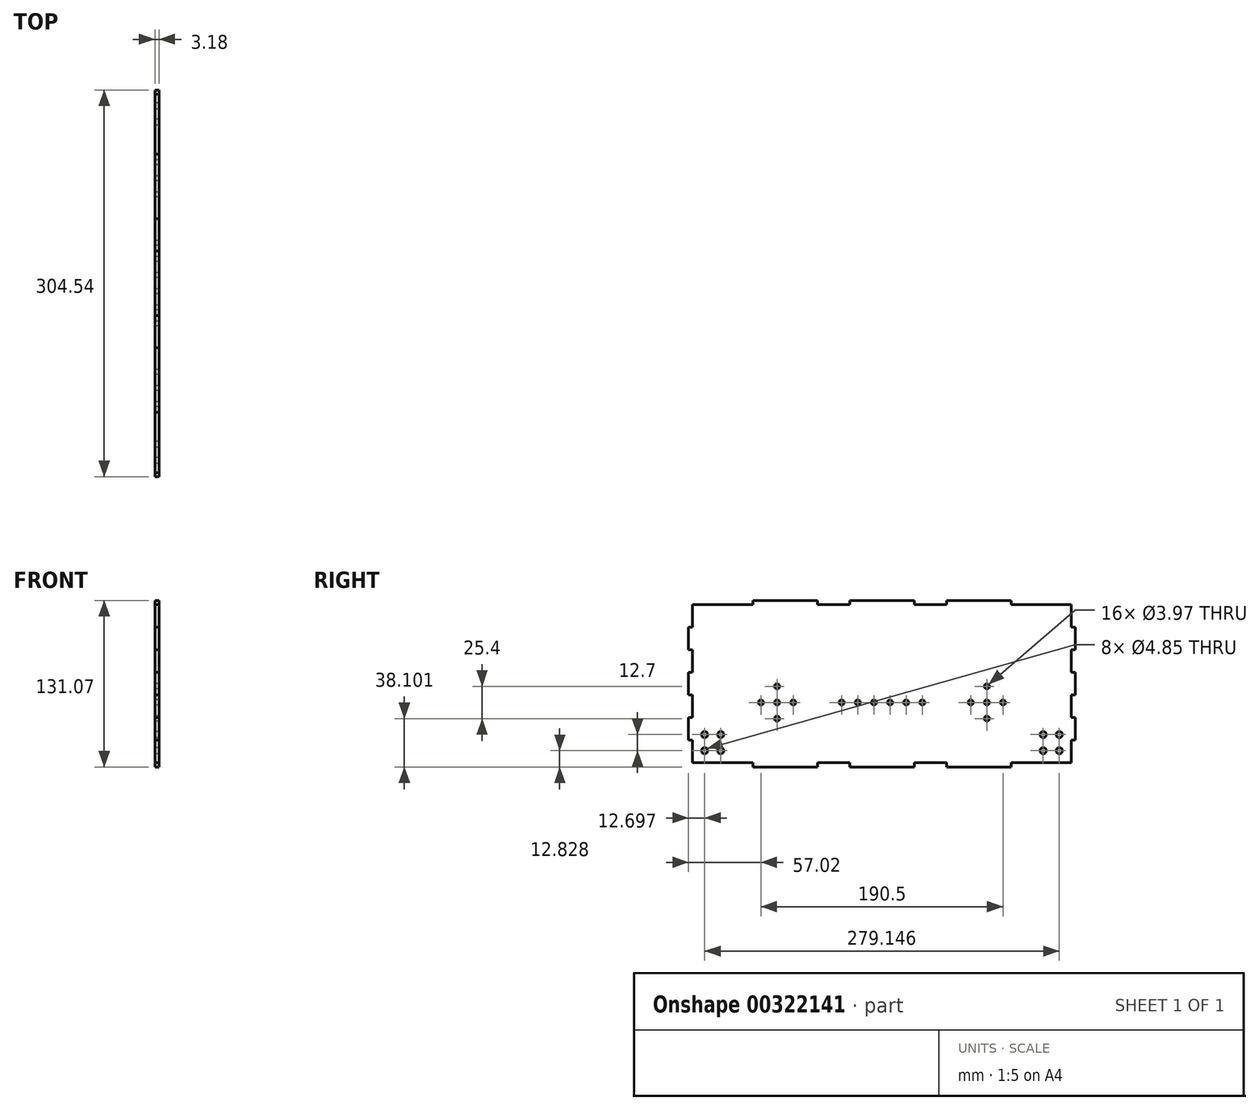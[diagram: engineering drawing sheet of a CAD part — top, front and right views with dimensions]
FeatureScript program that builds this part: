
annotation { "Feature Type Name" : "Feature", "Feature Type Description" : "" }
export const myFeature = defineFeature(function(context is Context, id is Id, definition is map)
    precondition{}
    {
        {
            var Q0;
            Q0=qCreatedBy(makeId("Right.planeOp"),FACE);
            var sketch = newSketch(context, id + "F0", { "sketchPlane" : qUnion([Q0])});
            skLineSegment(sketch, "E0.MirrorCS", {"start": v(-50.8, -81.48) * mm, "end": v(-50.8, -78.18) * mm});
            skLineSegment(sketch, "E1.MirrorCS", {"start": v(25.4, -81.48) * mm, "end": v(25.4, -78.18) * mm});
            skLineSegment(sketch, "E2.MirrorCS", {"start": v(50.8, -81.48) * mm, "end": v(50.8, -78.18) * mm});
            skLineSegment(sketch, "E3.MirrorCS", {"start": v(101.6, -81.48) * mm, "end": v(101.6, -78.18) * mm});
            skLineSegment(sketch, "E4.MirrorCS", {"start": v(-25.4, -81.48) * mm, "end": v(-25.4, -78.18) * mm});
            skLineSegment(sketch, "E5.MirrorCS", {"start": v(101.6, -81.48) * mm, "end": v(50.8, -81.48) * mm});
            skLineSegment(sketch, "E6.MirrorCS", {"start": v(-25.4, -81.48) * mm, "end": v(25.4, -81.48) * mm});
            skLineSegment(sketch, "E7.MirrorCS", {"start": v(-50.8, -81.48) * mm, "end": v(-25.4, -81.48) * mm, "construction": true});
            skLineSegment(sketch, "E8.MirrorCS", {"start": v(-101.6, -81.48) * mm, "end": v(-50.8, -81.48) * mm});
            skLineSegment(sketch, "E9.MirrorCS", {"start": v(-101.6, -81.48) * mm, "end": v(-101.6, -78.18) * mm});
            skLineSegment(sketch, "E10", {"start": v(101.6, -78.18) * mm, "end": v(149.1, -78.18) * mm});
            skLineSegment(sketch, "E11", {"start": v(50.8, -78.18) * mm, "end": v(25.4, -78.18) * mm});
            skLineSegment(sketch, "E12", {"start": v(-25.4, -78.18) * mm, "end": v(-50.8, -78.18) * mm});
            skLineSegment(sketch, "E13.MirrorCS", {"start": v(-101.6, -78.18) * mm, "end": v(-149.1, -78.18) * mm});
            skLineSegment(sketch, "E14", {"start": v(-149.1, -78.18) * mm, "end": v(-149.1, -60.4) * mm});
            skLineSegment(sketch, "E15", {"start": v(149.1, 46.28) * mm, "end": v(149.1, 28.5) * mm});
            skLineSegment(sketch, "E16", {"start": v(149.1, -15.95) * mm, "end": v(-149.1, -15.95) * mm, "construction": true});
            skLineSegment(sketch, "E17.MirrorCS", {"start": v(-50.8, 49.59) * mm, "end": v(-25.4, 49.59) * mm, "construction": true});
            skLineSegment(sketch, "E18.MirrorCS", {"start": v(-101.6, 49.59) * mm, "end": v(-101.6, 46.28) * mm});
            skLineSegment(sketch, "E19.MirrorCS", {"start": v(50.8, 46.28) * mm, "end": v(25.4, 46.28) * mm});
            skLineSegment(sketch, "E20.MirrorCS", {"start": v(25.4, 49.59) * mm, "end": v(25.4, 46.28) * mm});
            skLineSegment(sketch, "E21.MirrorCS", {"start": v(101.6, 49.59) * mm, "end": v(101.6, 46.28) * mm});
            skLineSegment(sketch, "E22.MirrorCS", {"start": v(101.6, 49.59) * mm, "end": v(50.8, 49.59) * mm});
            skLineSegment(sketch, "E23.MirrorCS", {"start": v(-101.6, 49.59) * mm, "end": v(-50.8, 49.59) * mm});
            skLineSegment(sketch, "E24.MirrorCS", {"start": v(-25.4, 46.28) * mm, "end": v(-50.8, 46.28) * mm});
            skLineSegment(sketch, "E25.MirrorCS", {"start": v(-101.6, 46.28) * mm, "end": v(-149.1, 46.28) * mm});
            skLineSegment(sketch, "E26.MirrorCS", {"start": v(101.6, 46.28) * mm, "end": v(149.1, 46.28) * mm});
            skLineSegment(sketch, "E27.MirrorCS", {"start": v(-50.8, 49.59) * mm, "end": v(-50.8, 46.28) * mm});
            skLineSegment(sketch, "E28.MirrorCS", {"start": v(50.8, 49.59) * mm, "end": v(50.8, 46.28) * mm});
            skLineSegment(sketch, "E29.MirrorCS", {"start": v(-25.4, 49.59) * mm, "end": v(-25.4, 46.28) * mm});
            skLineSegment(sketch, "E30.MirrorCS", {"start": v(-25.4, 49.59) * mm, "end": v(25.4, 49.59) * mm});
            skPoint(sketch, "E31", {"position": v(0, -30.68) * mm});
            skPoint(sketch, "E32", {"position": v(0, -15.95) * mm});
            skCircle(sketch, "E33", {"center": v(31.75, -30.68) * mm, "radius": 1.98 * mm});
            skCircle(sketch, "E34.MirrorC", {"center": v(-31.75, -30.68) * mm, "radius": 1.98 * mm});
            skCircle(sketch, "E35", {"center": v(82.55, -30.68) * mm, "radius": 1.98 * mm});
            skCircle(sketch, "E36.MirrorC", {"center": v(-82.55, -30.68) * mm, "radius": 1.98 * mm});
            skLineSegment(sketch, "E37", {"start": v(-149.1, 28.5) * mm, "end": v(-152.27, 28.5) * mm});
            skLineSegment(sketch, "E38", {"start": v(-152.27, 28.5) * mm, "end": v(-152.27, 10.72) * mm});
            skLineSegment(sketch, "E39", {"start": v(-152.27, 10.72) * mm, "end": v(-149.1, 10.72) * mm});
            skLineSegment(sketch, "E40", {"start": v(-149.1, -7.06) * mm, "end": v(-152.27, -7.06) * mm});
            skLineSegment(sketch, "E41", {"start": v(-152.27, -7.06) * mm, "end": v(-152.27, -24.84) * mm});
            skLineSegment(sketch, "E42", {"start": v(-152.27, -24.84) * mm, "end": v(-149.1, -24.84) * mm});
            skLineSegment(sketch, "E43", {"start": v(-149.1, -42.62) * mm, "end": v(-152.27, -42.62) * mm});
            skLineSegment(sketch, "E44", {"start": v(-152.27, -42.62) * mm, "end": v(-152.27, -60.4) * mm});
            skLineSegment(sketch, "E45", {"start": v(-152.27, -60.4) * mm, "end": v(-149.1, -60.4) * mm});
            skLineSegment(sketch, "E46", {"start": v(-152.27, 10.72) * mm, "end": v(-152.27, -7.06) * mm, "construction": true});
            skLineSegment(sketch, "E47", {"start": v(-152.27, -24.84) * mm, "end": v(-152.27, -42.62) * mm, "construction": true});
            skLineSegment(sketch, "E48", {"start": v(-152.27, 28.5) * mm, "end": v(-152.27, 46.28) * mm, "construction": true});
            skLineSegment(sketch, "E49", {"start": v(-152.27, -60.4) * mm, "end": v(-152.27, -78.18) * mm, "construction": true});
            skLineSegment(sketch, "E50.trimOffspring", {"start": v(-149.1, 28.5) * mm, "end": v(-149.1, 46.28) * mm});
            skLineSegment(sketch, "E51.trimOffspring", {"start": v(-149.1, -7.06) * mm, "end": v(-149.1, 10.72) * mm});
            skLineSegment(sketch, "E52.trimOffspring", {"start": v(-149.1, -42.62) * mm, "end": v(-149.1, -24.84) * mm});
            skLineSegment(sketch, "E53.MirrorCS", {"start": v(152.27, 10.72) * mm, "end": v(152.27, -7.06) * mm, "construction": true});
            skLineSegment(sketch, "E54.MirrorCS", {"start": v(149.1, -42.62) * mm, "end": v(149.1, -24.84) * mm});
            skLineSegment(sketch, "E55.MirrorCS", {"start": v(152.27, 28.5) * mm, "end": v(152.27, 10.72) * mm});
            skLineSegment(sketch, "E56.MirrorCS", {"start": v(152.27, -24.84) * mm, "end": v(152.27, -42.62) * mm, "construction": true});
            skLineSegment(sketch, "E57.MirrorCS", {"start": v(152.27, 10.72) * mm, "end": v(149.1, 10.72) * mm});
            skLineSegment(sketch, "E58.MirrorCS", {"start": v(149.1, -7.06) * mm, "end": v(152.27, -7.06) * mm});
            skLineSegment(sketch, "E59.MirrorCS", {"start": v(152.27, -7.06) * mm, "end": v(152.27, -24.84) * mm});
            skLineSegment(sketch, "E60.MirrorCS", {"start": v(152.27, -24.84) * mm, "end": v(149.1, -24.84) * mm});
            skLineSegment(sketch, "E61.MirrorCS", {"start": v(149.1, -42.62) * mm, "end": v(152.27, -42.62) * mm});
            skLineSegment(sketch, "E62.MirrorCS", {"start": v(149.1, -7.06) * mm, "end": v(149.1, 10.72) * mm});
            skLineSegment(sketch, "E63.MirrorCS", {"start": v(152.27, -42.62) * mm, "end": v(152.27, -60.4) * mm});
            skLineSegment(sketch, "E64.MirrorCS", {"start": v(152.27, -60.4) * mm, "end": v(149.1, -60.4) * mm});
            skLineSegment(sketch, "E65.MirrorCS", {"start": v(149.1, 28.5) * mm, "end": v(152.27, 28.5) * mm});
            skLineSegment(sketch, "E66.trimOffspring", {"start": v(149.1, 10.72) * mm, "end": v(149.1, -7.06) * mm});
            skPoint(sketch, "E67.orphan", {"position": v(149.1, -15.95) * mm});
            skLineSegment(sketch, "E68.trimOffspring", {"start": v(149.1, -15.95) * mm, "end": v(149.1, -42.62) * mm});
            skLineSegment(sketch, "E69.trimOffspring", {"start": v(149.1, -60.4) * mm, "end": v(149.1, -78.18) * mm});
            skCircle(sketch, "E70", {"center": v(19.05, -30.68) * mm, "radius": 1.98 * mm});
            skCircle(sketch, "E71", {"center": v(6.35, -30.68) * mm, "radius": 1.98 * mm});
            skCircle(sketch, "E72", {"center": v(-19.05, -30.68) * mm, "radius": 1.98 * mm});
            skCircle(sketch, "E73", {"center": v(-6.35, -30.68) * mm, "radius": 1.98 * mm});
            skCircle(sketch, "E74", {"center": v(-139.57, -68.65) * mm, "radius": 2.42 * mm});
            skCircle(sketch, "E75", {"center": v(-126.87, -68.65) * mm, "radius": 2.42 * mm});
            skCircle(sketch, "E76", {"center": v(-126.87, -55.95) * mm, "radius": 2.42 * mm});
            skCircle(sketch, "E77", {"center": v(-139.57, -55.95) * mm, "radius": 2.42 * mm});
            skCircle(sketch, "E78.MirrorC", {"center": v(126.87, -55.95) * mm, "radius": 2.42 * mm});
            skCircle(sketch, "E79.MirrorC", {"center": v(126.87, -68.65) * mm, "radius": 2.42 * mm});
            skCircle(sketch, "E80.MirrorC", {"center": v(139.57, -68.65) * mm, "radius": 2.42 * mm});
            skCircle(sketch, "E81.MirrorC", {"center": v(139.57, -55.95) * mm, "radius": 2.42 * mm});
            skCircle(sketch, "E82", {"center": v(-95.25, -30.68) * mm, "radius": 1.98 * mm});
            skCircle(sketch, "E83.1.0", {"center": v(-82.55, -43.38) * mm, "radius": 1.98 * mm});
            skCircle(sketch, "E83.2.0", {"center": v(-69.85, -30.68) * mm, "radius": 1.98 * mm});
            skCircle(sketch, "E83.3.0", {"center": v(-82.55, -17.98) * mm, "radius": 1.98 * mm});
            skCircle(sketch, "E84.MirrorC", {"center": v(82.55, -17.98) * mm, "radius": 1.98 * mm});
            skCircle(sketch, "E85.MirrorC", {"center": v(95.25, -30.68) * mm, "radius": 1.98 * mm});
            skCircle(sketch, "E86.MirrorC", {"center": v(69.85, -30.68) * mm, "radius": 1.98 * mm});
            skCircle(sketch, "E87.MirrorC", {"center": v(82.55, -43.38) * mm, "radius": 1.98 * mm});
            skSolve(sketch);
        }
        {
            var Q0;
            Q0=makeQuery(id+"F0.imprint","IMPRINT",FACE,{"disambiguationData":[TD([[makeQuery(id+"F0.imprint","IMPRINT",EDGE,{"derivedFrom":sQuery(id+"F0.wireOp",EDGE,"E0.MirrorCS")}),1.0]])]});
            extrude(context, id + "F1", {"entities" : qUnion([Q0]), "depth" : 3.17 * mm});
        }
    });
